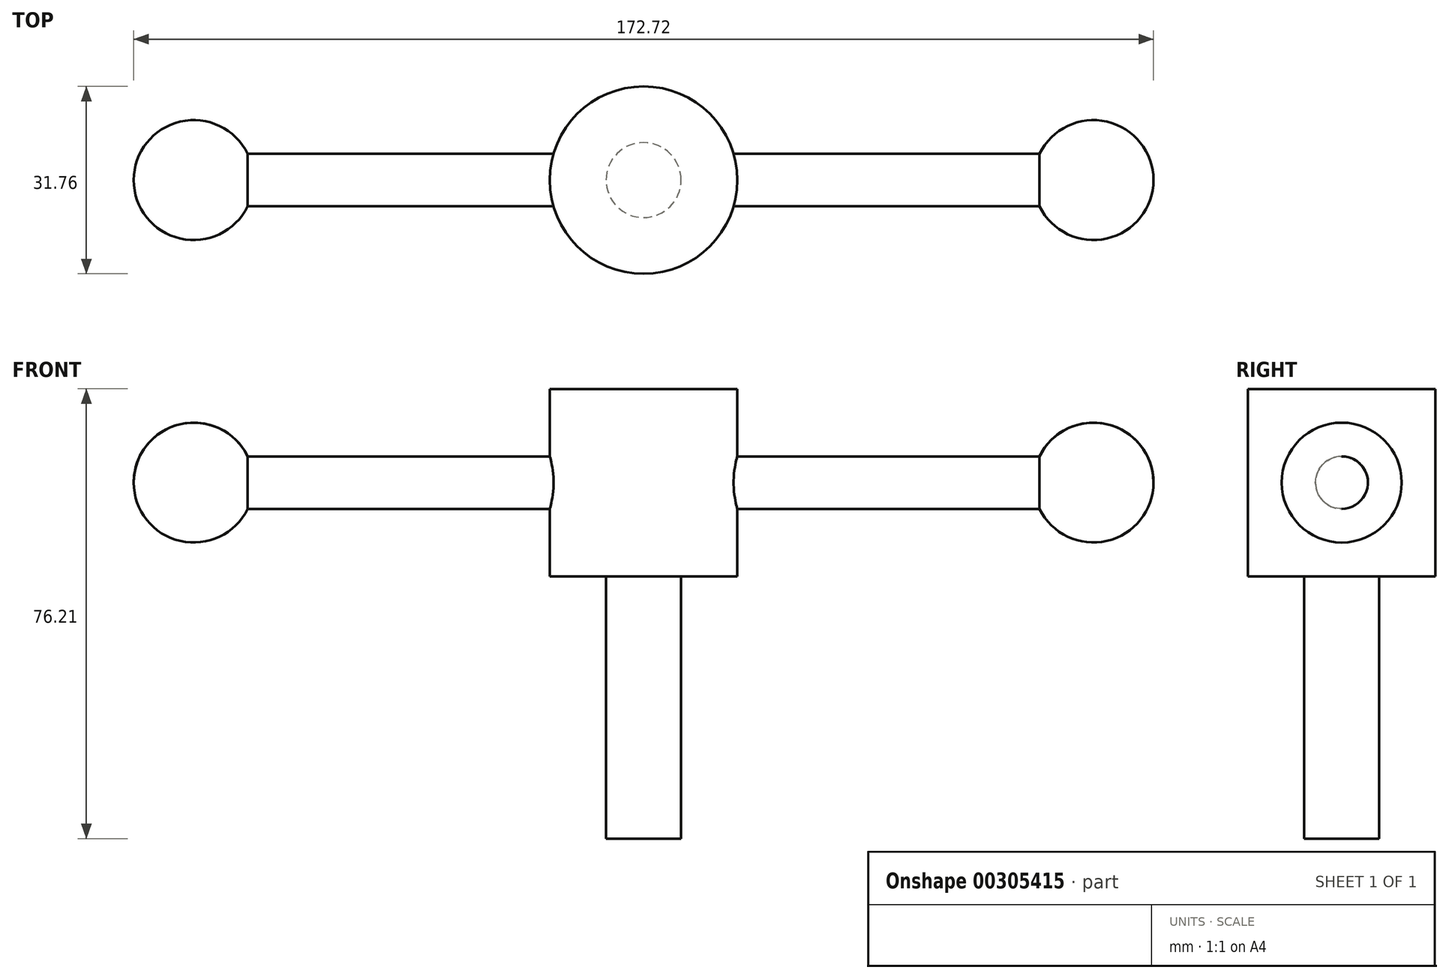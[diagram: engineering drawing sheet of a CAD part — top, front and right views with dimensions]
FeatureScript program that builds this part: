
annotation { "Feature Type Name" : "Feature", "Feature Type Description" : "" }
export const myFeature = defineFeature(function(context is Context, id is Id, definition is map)
    precondition{}
    {
        {
            var Q0;
            Q0=qCreatedBy(makeId("Front.planeOp"),FACE);
            var sketch = newSketch(context, id + "F0", { "sketchPlane" : qUnion([Q0])});
            skArc(sketch, "E0", {"start": v(-66.04, 25.4) * mm, "mid": v(-76.2, 35.56) * mm, "end": v(-86.36, 25.4) * mm});
            skArc(sketch, "E1", {"start": v(86.36, 25.4) * mm, "mid": v(76.2, 35.56) * mm, "end": v(66.04, 25.4) * mm});
            skPoint(sketch, "E2", {"position": v(0, 25.4) * mm});
            skLineSegment(sketch, "E3", {"start": v(-86.36, 25.4) * mm, "end": v(-66.04, 25.4) * mm});
            skLineSegment(sketch, "E4", {"start": v(66.04, 25.4) * mm, "end": v(86.36, 25.4) * mm});
            skSolve(sketch);
        }
        {
            var Q0;
            Q0 = qSketchRegion(id + "F0", true);
            var Q1;
            Q1=sQuery(id+"F0.wireOp",EDGE,"E3");
            revolve(context, id + "F1", {"entities" : qUnion([Q0]), "axis" : qUnion([Q1]), "revolveType" : RevolveType.FULL});
        }
        {
            var Q0;
            Q0=qCreatedBy(makeId("Front.planeOp"),FACE);
            var sketch = newSketch(context, id + "F2", { "sketchPlane" : qUnion([Q0])});
            skLineSegment(sketch, "E5.bottom", {"start": v(0, 9.53) * mm, "end": v(15.87, 9.53) * mm});
            skLineSegment(sketch, "E5.top", {"start": v(0, 41.28) * mm, "end": v(15.87, 41.28) * mm});
            skLineSegment(sketch, "E5.right", {"start": v(15.88, 9.53) * mm, "end": v(15.87, 41.28) * mm});
            skLineSegment(sketch, "E6", {"start": v(0, 41.28) * mm, "end": v(0, 9.53) * mm});
            skPoint(sketch, "E7", {"position": v(0, 25.4) * mm});
            skPoint(sketch, "E8.start.orphan", {"position": v(15.88, 25.4) * mm});
            skSolve(sketch);
        }
        {
            var Q0;
            Q0=qCreatedBy(makeId("Front.planeOp"),FACE);
            var sketch = newSketch(context, id + "F3", { "sketchPlane" : qUnion([Q0])});
            skLineSegment(sketch, "E9", {"start": v(-76.2, 25.4) * mm, "end": v(76.2, 25.4) * mm});
            skPoint(sketch, "E10", {"position": v(0, 25.4) * mm});
            skLineSegment(sketch, "E11", {"start": v(-76.2, 25.4) * mm, "end": v(-76.2, 29.84) * mm});
            skLineSegment(sketch, "E12", {"start": v(-76.2, 29.84) * mm, "end": v(76.2, 29.84) * mm});
            skLineSegment(sketch, "E13", {"start": v(76.2, 29.84) * mm, "end": v(76.2, 25.4) * mm});
            skSolve(sketch);
        }
        {
            var Q0;
            Q0 = qSketchRegion(id + "F3", true);
            var Q1;
            Q1=sQuery(id+"F3.wireOp",EDGE,"E9");
            revolve(context, id + "F4", {"operationType" : NewBodyOperationType.ADD, "entities" : qUnion([Q0]), "axis" : qUnion([Q1]), "revolveType" : RevolveType.FULL});
        }
        {
            var Q0;
            Q0 = qSketchRegion(id + "F2", true);
            var Q1;
            Q1=sQuery(id+"F2.wireOp",EDGE,"E6");
            revolve(context, id + "F5", {"operationType" : NewBodyOperationType.ADD, "entities" : qUnion([Q0]), "axis" : qUnion([Q1]), "revolveType" : RevolveType.FULL});
        }
        {
            var Q0;
            Q0=makeQuery(id+"F5.opRevolve","SWEPT_FACE",FACE,{"disambiguationData":[OSD([sQuery(id+"F2.wireOp",EDGE,"E5.bottom")])]});
            var sketch = newSketch(context, id + "F6", { "sketchPlane" : qUnion([Q0])});
            skCircle(sketch, "E14", {"center": v(0, 0) * mm, "radius": 6.35 * mm});
            skSolve(sketch);
        }
        {
            var Q0;
            Q0 = qSketchRegion(id + "F6", true);
            extrude(context, id + "F7", {"entities" : qUnion([Q0]), "operationType" : NewBodyOperationType.ADD, "depth" : 44.45 * mm});
        }
    });
